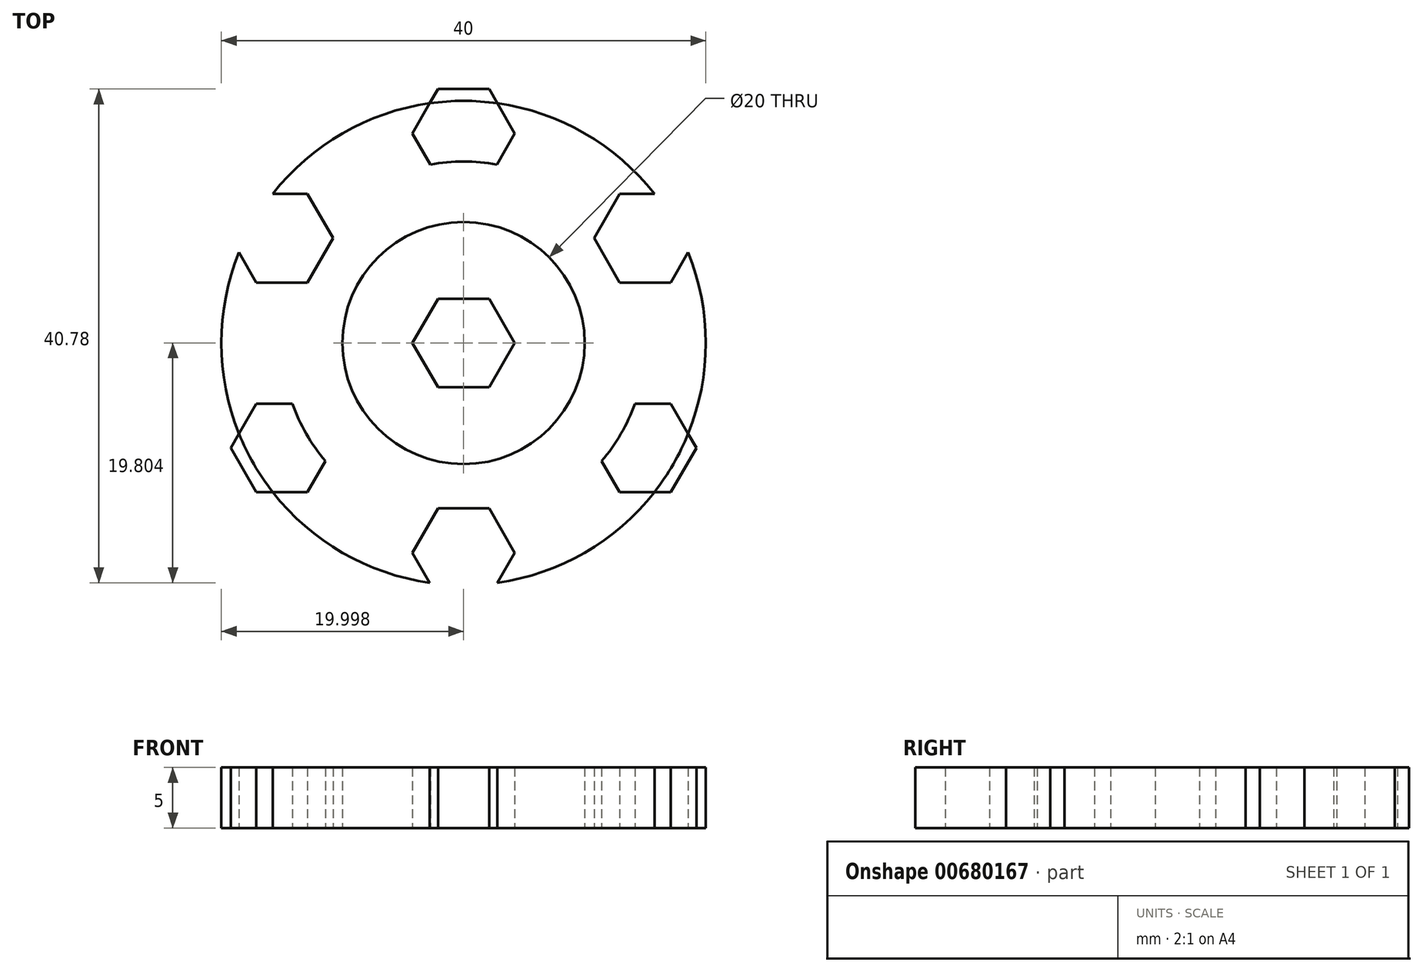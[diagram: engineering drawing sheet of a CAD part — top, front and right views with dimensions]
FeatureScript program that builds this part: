
annotation { "Feature Type Name" : "Feature", "Feature Type Description" : "" }
export const myFeature = defineFeature(function(context is Context, id is Id, definition is map)
    precondition{}
    {
        {
            var Q0;
            Q0=qCreatedBy(makeId("Top.planeOp"),FACE);
            var sketch = newSketch(context, id + "F0", { "sketchPlane" : qUnion([Q0])});
            skLineSegment(sketch, "E0.0", {"start": v(-11.35, 1.25) * mm, "end": v(-21.35, 1.25) * mm});
            skLineSegment(sketch, "E0.1", {"start": v(-21.35, 1.25) * mm, "end": v(-26.35, 9.91) * mm});
            skLineSegment(sketch, "E0.2", {"start": v(-26.35, 9.91) * mm, "end": v(-21.35, 18.57) * mm});
            skLineSegment(sketch, "E0.3", {"start": v(-21.35, 18.57) * mm, "end": v(-11.35, 18.57) * mm});
            skLineSegment(sketch, "E0.4", {"start": v(-11.35, 18.57) * mm, "end": v(-6.35, 9.91) * mm});
            skLineSegment(sketch, "E0.5", {"start": v(-6.35, 9.91) * mm, "end": v(-11.35, 1.25) * mm});
            skPoint(sketch, "E0.0.midPoint", {"position": v(-16.35, 1.25) * mm});
            skLineSegment(sketch, "E1", {"start": v(-21.35, 1.25) * mm, "end": v(-11.35, 1.25) * mm});
            skLineSegment(sketch, "E2", {"start": v(-11.35, 1.25) * mm, "end": v(-6.35, 9.91) * mm});
            skLineSegment(sketch, "E3", {"start": v(-6.35, 9.91) * mm, "end": v(-11.35, 18.57) * mm});
            skLineSegment(sketch, "E4", {"start": v(-11.35, 18.57) * mm, "end": v(-21.35, 18.57) * mm});
            skLineSegment(sketch, "E5", {"start": v(-21.35, 18.57) * mm, "end": v(-26.35, 9.91) * mm});
            skLineSegment(sketch, "E6", {"start": v(-26.35, 9.91) * mm, "end": v(-21.35, 1.25) * mm});
            skLineSegment(sketch, "E7.MirrorCS", {"start": v(-6.35, 27.23) * mm, "end": v(-11.35, 35.9) * mm});
            skLineSegment(sketch, "E8.MirrorCS", {"start": v(-21.35, 35.9) * mm, "end": v(-26.35, 27.23) * mm});
            skLineSegment(sketch, "E9.MirrorCS", {"start": v(-26.35, 27.23) * mm, "end": v(-21.35, 18.57) * mm});
            skLineSegment(sketch, "E10.MirrorCS", {"start": v(-11.35, 35.9) * mm, "end": v(-6.35, 27.23) * mm});
            skLineSegment(sketch, "E11.MirrorCS", {"start": v(-11.35, 35.9) * mm, "end": v(-21.35, 35.9) * mm});
            skLineSegment(sketch, "E12.MirrorCS", {"start": v(-11.35, 18.57) * mm, "end": v(-6.35, 27.23) * mm});
            skLineSegment(sketch, "E13.MirrorCS", {"start": v(-21.35, 35.9) * mm, "end": v(-11.35, 35.9) * mm});
            skLineSegment(sketch, "E14.MirrorCS", {"start": v(-6.35, 27.23) * mm, "end": v(-11.35, 18.57) * mm});
            skLineSegment(sketch, "E15.MirrorCS", {"start": v(-26.35, 27.23) * mm, "end": v(-21.35, 35.9) * mm});
            skLineSegment(sketch, "E16.MirrorCS", {"start": v(-21.35, 18.57) * mm, "end": v(-26.35, 27.23) * mm});
            skPoint(sketch, "E17.MirrorP", {"position": v(-16.35, 35.9) * mm});
            skLineSegment(sketch, "E18.MirrorCS", {"start": v(-6.35, 9.91) * mm, "end": v(3.65, 9.91) * mm});
            skLineSegment(sketch, "E19.MirrorCS", {"start": v(3.65, 9.91) * mm, "end": v(8.65, 18.57) * mm});
            skLineSegment(sketch, "E20.MirrorCS", {"start": v(8.65, 18.57) * mm, "end": v(3.65, 27.23) * mm});
            skLineSegment(sketch, "E21.MirrorCS", {"start": v(3.65, 27.23) * mm, "end": v(-6.35, 27.23) * mm});
            skLineSegment(sketch, "E22.MirrorCS", {"start": v(3.65, 9.91) * mm, "end": v(-6.35, 9.91) * mm});
            skPoint(sketch, "E23.MirrorP", {"position": v(6.15, 14.24) * mm});
            skLineSegment(sketch, "E24.MirrorCS", {"start": v(-6.35, 27.23) * mm, "end": v(3.65, 27.23) * mm});
            skLineSegment(sketch, "E25.MirrorCS", {"start": v(8.65, 18.57) * mm, "end": v(3.65, 9.91) * mm});
            skLineSegment(sketch, "E26.MirrorCS", {"start": v(3.65, 27.23) * mm, "end": v(8.65, 18.57) * mm});
            skLineSegment(sketch, "E27.MirrorCS", {"start": v(8.65, 1.25) * mm, "end": v(3.65, 9.91) * mm});
            skLineSegment(sketch, "E28.MirrorCS", {"start": v(3.65, -7.4) * mm, "end": v(8.65, 1.25) * mm});
            skLineSegment(sketch, "E29.MirrorCS", {"start": v(-6.35, -7.4) * mm, "end": v(3.65, -7.4) * mm});
            skLineSegment(sketch, "E30.MirrorCS", {"start": v(-11.35, 1.25) * mm, "end": v(-6.35, -7.4) * mm});
            skLineSegment(sketch, "E31.MirrorCS", {"start": v(3.65, 9.91) * mm, "end": v(8.65, 1.25) * mm});
            skPoint(sketch, "E32.MirrorP", {"position": v(-8.85, -3.08) * mm});
            skLineSegment(sketch, "E33.MirrorCS", {"start": v(3.65, -7.4) * mm, "end": v(-6.35, -7.4) * mm});
            skLineSegment(sketch, "E34.MirrorCS", {"start": v(-6.35, -7.4) * mm, "end": v(-11.35, 1.25) * mm});
            skLineSegment(sketch, "E35.MirrorCS", {"start": v(8.65, 1.25) * mm, "end": v(3.65, -7.4) * mm});
            skLineSegment(sketch, "E36.MirrorCS", {"start": v(-11.35, -16.07) * mm, "end": v(-6.35, -7.4) * mm});
            skLineSegment(sketch, "E37.MirrorCS", {"start": v(-6.35, -7.4) * mm, "end": v(-11.35, -16.07) * mm});
            skLineSegment(sketch, "E38.MirrorCS", {"start": v(-21.35, -16.07) * mm, "end": v(-11.35, -16.07) * mm});
            skLineSegment(sketch, "E39.MirrorCS", {"start": v(-21.35, 1.25) * mm, "end": v(-26.35, -7.4) * mm});
            skLineSegment(sketch, "E40.MirrorCS", {"start": v(-26.35, -7.4) * mm, "end": v(-21.35, -16.07) * mm});
            skLineSegment(sketch, "E41.MirrorCS", {"start": v(-11.35, -16.07) * mm, "end": v(-21.35, -16.07) * mm});
            skLineSegment(sketch, "E42.MirrorCS", {"start": v(-26.35, -7.4) * mm, "end": v(-21.35, 1.25) * mm});
            skLineSegment(sketch, "E43.MirrorCS", {"start": v(-21.35, -16.07) * mm, "end": v(-26.35, -7.4) * mm});
            skLineSegment(sketch, "E44.MirrorCS", {"start": v(-36.35, -7.4) * mm, "end": v(-26.35, -7.4) * mm});
            skLineSegment(sketch, "E45.MirrorCS", {"start": v(-41.35, 1.25) * mm, "end": v(-36.35, -7.4) * mm});
            skLineSegment(sketch, "E46.MirrorCS", {"start": v(-36.35, -7.4) * mm, "end": v(-41.35, 1.25) * mm});
            skLineSegment(sketch, "E47.MirrorCS", {"start": v(-26.35, -7.4) * mm, "end": v(-36.35, -7.4) * mm});
            skLineSegment(sketch, "E48.MirrorCS", {"start": v(-36.35, 9.91) * mm, "end": v(-41.35, 1.25) * mm});
            skLineSegment(sketch, "E49.MirrorCS", {"start": v(-41.35, 1.25) * mm, "end": v(-36.35, 9.91) * mm});
            skLineSegment(sketch, "E50.MirrorCS", {"start": v(-26.35, 9.91) * mm, "end": v(-36.35, 9.91) * mm});
            skLineSegment(sketch, "E51.MirrorCS", {"start": v(-36.35, 9.91) * mm, "end": v(-26.35, 9.91) * mm});
            skLineSegment(sketch, "E52.MirrorCS", {"start": v(-26.35, 27.23) * mm, "end": v(-36.35, 27.23) * mm});
            skLineSegment(sketch, "E53.MirrorCS", {"start": v(-36.35, 27.23) * mm, "end": v(-41.35, 18.57) * mm});
            skLineSegment(sketch, "E54.MirrorCS", {"start": v(-41.35, 18.57) * mm, "end": v(-36.35, 9.91) * mm});
            skLineSegment(sketch, "E55.MirrorCS", {"start": v(-41.35, 18.57) * mm, "end": v(-36.35, 27.23) * mm});
            skLineSegment(sketch, "E56.MirrorCS", {"start": v(-36.35, 27.23) * mm, "end": v(-26.35, 27.23) * mm});
            skPoint(sketch, "E57.MirrorP", {"position": v(-38.85, 14.24) * mm});
            skLineSegment(sketch, "E58.MirrorCS", {"start": v(-36.35, 9.91) * mm, "end": v(-41.35, 18.57) * mm});
            skLineSegment(sketch, "E59.MirrorCS", {"start": v(-26.35, 44.55) * mm, "end": v(-36.35, 44.55) * mm});
            skLineSegment(sketch, "E60.MirrorCS", {"start": v(-41.35, 35.9) * mm, "end": v(-36.35, 27.23) * mm});
            skLineSegment(sketch, "E61.MirrorCS", {"start": v(-36.35, 44.55) * mm, "end": v(-26.35, 44.55) * mm});
            skLineSegment(sketch, "E62.MirrorCS", {"start": v(-26.35, 44.55) * mm, "end": v(-21.35, 35.9) * mm});
            skLineSegment(sketch, "E63.MirrorCS", {"start": v(-36.35, 44.55) * mm, "end": v(-41.35, 35.9) * mm});
            skLineSegment(sketch, "E64.MirrorCS", {"start": v(-36.35, 27.23) * mm, "end": v(-41.35, 35.9) * mm});
            skLineSegment(sketch, "E65.MirrorCS", {"start": v(-21.35, 35.9) * mm, "end": v(-26.35, 44.55) * mm});
            skPoint(sketch, "E66.MirrorP", {"position": v(-38.85, 40.22) * mm});
            skLineSegment(sketch, "E67.MirrorCS", {"start": v(-41.35, 35.9) * mm, "end": v(-36.35, 44.55) * mm});
            skLineSegment(sketch, "E68.MirrorCS", {"start": v(-56.35, 9.91) * mm, "end": v(-51.35, 18.57) * mm});
            skLineSegment(sketch, "E69.MirrorCS", {"start": v(-41.35, 1.25) * mm, "end": v(-51.35, 1.25) * mm});
            skLineSegment(sketch, "E70.MirrorCS", {"start": v(-56.35, 9.91) * mm, "end": v(-51.35, 1.25) * mm});
            skLineSegment(sketch, "E71.MirrorCS", {"start": v(-51.35, 1.25) * mm, "end": v(-56.35, 9.91) * mm});
            skLineSegment(sketch, "E72.MirrorCS", {"start": v(-51.35, 18.57) * mm, "end": v(-56.35, 9.91) * mm});
            skLineSegment(sketch, "E73.MirrorCS", {"start": v(-51.35, 18.57) * mm, "end": v(-41.35, 18.57) * mm});
            skLineSegment(sketch, "E74.MirrorCS", {"start": v(-41.35, 18.57) * mm, "end": v(-51.35, 18.57) * mm});
            skLineSegment(sketch, "E75.MirrorCS", {"start": v(-51.35, 1.25) * mm, "end": v(-41.35, 1.25) * mm});
            skLineSegment(sketch, "E76.MirrorCS", {"start": v(-6.35, 44.55) * mm, "end": v(3.65, 44.55) * mm});
            skLineSegment(sketch, "E77.MirrorCS", {"start": v(3.65, 44.55) * mm, "end": v(-6.35, 44.55) * mm});
            skLineSegment(sketch, "E78.MirrorCS", {"start": v(8.65, 35.9) * mm, "end": v(3.65, 44.55) * mm});
            skLineSegment(sketch, "E79.MirrorCS", {"start": v(3.65, 44.55) * mm, "end": v(8.65, 35.9) * mm});
            skLineSegment(sketch, "E80.MirrorCS", {"start": v(8.65, 35.9) * mm, "end": v(3.65, 27.23) * mm});
            skLineSegment(sketch, "E81.MirrorCS", {"start": v(3.65, 27.23) * mm, "end": v(8.65, 35.9) * mm});
            skLineSegment(sketch, "E82.MirrorCS", {"start": v(-6.35, 44.55) * mm, "end": v(-11.35, 35.9) * mm});
            skLineSegment(sketch, "E83.MirrorCS", {"start": v(-11.35, 35.9) * mm, "end": v(-6.35, 44.55) * mm});
            skPoint(sketch, "E84.MirrorP", {"position": v(-8.85, 40.22) * mm});
            skLineSegment(sketch, "E85.MirrorCS", {"start": v(23.65, 9.91) * mm, "end": v(18.65, 18.57) * mm});
            skLineSegment(sketch, "E86.MirrorCS", {"start": v(18.65, 1.25) * mm, "end": v(23.65, 9.91) * mm});
            skLineSegment(sketch, "E87.MirrorCS", {"start": v(18.65, 18.57) * mm, "end": v(23.65, 9.91) * mm});
            skLineSegment(sketch, "E88.MirrorCS", {"start": v(23.65, 9.91) * mm, "end": v(18.65, 1.25) * mm});
            skLineSegment(sketch, "E89.MirrorCS", {"start": v(18.65, 1.25) * mm, "end": v(8.65, 1.25) * mm});
            skLineSegment(sketch, "E90.MirrorCS", {"start": v(18.65, 18.57) * mm, "end": v(8.65, 18.57) * mm});
            skLineSegment(sketch, "E91.MirrorCS", {"start": v(8.65, 1.25) * mm, "end": v(18.65, 1.25) * mm});
            skLineSegment(sketch, "E92.MirrorCS", {"start": v(8.65, 18.57) * mm, "end": v(18.65, 18.57) * mm});
            skLineSegment(sketch, "E93.MirrorCS", {"start": v(8.65, -16.07) * mm, "end": v(3.65, -24.73) * mm});
            skLineSegment(sketch, "E94.MirrorCS", {"start": v(3.65, -24.73) * mm, "end": v(8.65, -16.07) * mm});
            skLineSegment(sketch, "E95.MirrorCS", {"start": v(3.65, -24.73) * mm, "end": v(-6.35, -24.73) * mm});
            skLineSegment(sketch, "E96.MirrorCS", {"start": v(-6.35, -24.73) * mm, "end": v(3.65, -24.73) * mm});
            skLineSegment(sketch, "E97.MirrorCS", {"start": v(-6.35, -24.73) * mm, "end": v(-11.35, -16.07) * mm});
            skLineSegment(sketch, "E98.MirrorCS", {"start": v(-11.35, -16.07) * mm, "end": v(-6.35, -24.73) * mm});
            skPoint(sketch, "E99.MirrorP", {"position": v(-16.35, -16.07) * mm});
            skLineSegment(sketch, "E100.MirrorCS", {"start": v(8.65, -16.07) * mm, "end": v(3.65, -7.4) * mm});
            skPoint(sketch, "E101.MirrorP", {"position": v(-8.85, -11.74) * mm});
            skLineSegment(sketch, "E102.MirrorCS", {"start": v(3.65, -7.4) * mm, "end": v(8.65, -16.07) * mm});
            skLineSegment(sketch, "E103.MirrorCS", {"start": v(-26.35, -24.73) * mm, "end": v(-36.35, -24.73) * mm});
            skLineSegment(sketch, "E104.MirrorCS", {"start": v(-36.35, -24.73) * mm, "end": v(-26.35, -24.73) * mm});
            skLineSegment(sketch, "E105.MirrorCS", {"start": v(-36.35, -24.73) * mm, "end": v(-41.35, -16.07) * mm});
            skLineSegment(sketch, "E106.MirrorCS", {"start": v(-41.35, -16.07) * mm, "end": v(-36.35, -24.73) * mm});
            skLineSegment(sketch, "E107.MirrorCS", {"start": v(-41.35, -16.07) * mm, "end": v(-36.35, -7.4) * mm});
            skLineSegment(sketch, "E108.MirrorCS", {"start": v(-26.35, -24.73) * mm, "end": v(-21.35, -16.07) * mm});
            skPoint(sketch, "E109.MirrorP", {"position": v(-38.85, -11.74) * mm});
            skLineSegment(sketch, "E110.MirrorCS", {"start": v(-21.35, -16.07) * mm, "end": v(-26.35, -24.73) * mm});
            skPoint(sketch, "E111.MirrorP", {"position": v(-23.85, -20.4) * mm});
            skLineSegment(sketch, "E112.MirrorCS", {"start": v(-36.35, -7.4) * mm, "end": v(-41.35, -16.07) * mm});
            skPoint(sketch, "E113.MirrorP", {"position": v(-38.85, -20.4) * mm});
            skPoint(sketch, "E114.MirrorP", {"position": v(-31.35, -24.73) * mm});
            skLineSegment(sketch, "E115", {"start": v(-11.35, 18.57) * mm, "end": v(-21.35, 1.25) * mm});
            skLineSegment(sketch, "E116", {"start": v(-26.35, 9.91) * mm, "end": v(-6.35, 9.91) * mm});
            skLineSegment(sketch, "E117", {"start": v(-11.35, 1.25) * mm, "end": v(-21.35, 18.57) * mm});
            skPoint(sketch, "E118", {"position": v(-16.35, 9.91) * mm});
            skCircle(sketch, "E119", {"center": v(-16.35, 9.91) * mm, "radius": 15 * mm});
            skPoint(sketch, "E120", {"position": v(-31.35, 9.91) * mm});
            skPoint(sketch, "E121", {"position": v(-1.35, 9.91) * mm});
            skPoint(sketch, "E122", {"position": v(-23.85, -3.08) * mm});
            skPoint(sketch, "E123", {"position": v(-23.85, 22.9) * mm});
            skPoint(sketch, "E124", {"position": v(-8.85, 22.9) * mm});
            skLineSegment(sketch, "E125.0", {"start": v(-3.47, 39.55) * mm, "end": v(0.76, 39.55) * mm});
            skLineSegment(sketch, "E125.1", {"start": v(2.87, 35.9) * mm, "end": v(0.76, 32.23) * mm});
            skLineSegment(sketch, "E125.2", {"start": v(0.76, 32.23) * mm, "end": v(-3.47, 32.23) * mm});
            skLineSegment(sketch, "E125.3", {"start": v(0.76, 39.55) * mm, "end": v(2.87, 35.9) * mm});
            skLineSegment(sketch, "E125.4", {"start": v(-3.47, 32.23) * mm, "end": v(-5.58, 35.9) * mm});
            skLineSegment(sketch, "E125.5", {"start": v(-5.58, 35.9) * mm, "end": v(-3.47, 39.55) * mm});
            skLineSegment(sketch, "E126.0", {"start": v(0.76, 22.23) * mm, "end": v(-3.47, 22.23) * mm});
            skLineSegment(sketch, "E126.1", {"start": v(2.87, 18.57) * mm, "end": v(0.76, 14.91) * mm});
            skLineSegment(sketch, "E126.2", {"start": v(-3.47, 14.91) * mm, "end": v(0.76, 14.91) * mm});
            skLineSegment(sketch, "E126.3", {"start": v(0.76, 22.23) * mm, "end": v(2.87, 18.57) * mm});
            skLineSegment(sketch, "E126.4", {"start": v(-3.47, 14.91) * mm, "end": v(-5.58, 18.57) * mm});
            skLineSegment(sketch, "E126.5", {"start": v(-5.58, 18.57) * mm, "end": v(-3.47, 22.23) * mm});
            skLineSegment(sketch, "E127.0", {"start": v(-18.47, 30.9) * mm, "end": v(-20.58, 27.23) * mm});
            skLineSegment(sketch, "E127.1", {"start": v(-12.13, 27.23) * mm, "end": v(-14.24, 30.9) * mm});
            skLineSegment(sketch, "E127.2", {"start": v(-14.24, 23.57) * mm, "end": v(-12.13, 27.23) * mm});
            skLineSegment(sketch, "E127.3", {"start": v(-18.47, 30.9) * mm, "end": v(-14.24, 30.9) * mm});
            skLineSegment(sketch, "E127.4", {"start": v(-14.24, 23.57) * mm, "end": v(-18.47, 23.57) * mm});
            skLineSegment(sketch, "E127.5", {"start": v(-20.58, 27.23) * mm, "end": v(-18.47, 23.57) * mm});
            skLineSegment(sketch, "E128.0", {"start": v(-29.24, 39.55) * mm, "end": v(-27.13, 35.9) * mm});
            skLineSegment(sketch, "E128.1", {"start": v(-33.47, 32.23) * mm, "end": v(-29.24, 32.23) * mm});
            skLineSegment(sketch, "E128.2", {"start": v(-35.58, 35.9) * mm, "end": v(-33.47, 32.23) * mm});
            skLineSegment(sketch, "E128.3", {"start": v(-27.13, 35.9) * mm, "end": v(-29.24, 32.23) * mm});
            skLineSegment(sketch, "E128.4", {"start": v(-35.58, 35.9) * mm, "end": v(-33.47, 39.55) * mm});
            skLineSegment(sketch, "E128.5", {"start": v(-33.47, 39.55) * mm, "end": v(-29.24, 39.55) * mm});
            skLineSegment(sketch, "E129.0", {"start": v(17.87, 9.91) * mm, "end": v(15.76, 13.57) * mm});
            skLineSegment(sketch, "E129.1", {"start": v(11.53, 13.57) * mm, "end": v(9.42, 9.91) * mm});
            skLineSegment(sketch, "E129.2", {"start": v(9.42, 9.91) * mm, "end": v(11.53, 6.25) * mm});
            skLineSegment(sketch, "E129.3", {"start": v(15.76, 13.57) * mm, "end": v(11.53, 13.57) * mm});
            skLineSegment(sketch, "E129.4", {"start": v(11.53, 6.25) * mm, "end": v(15.76, 6.25) * mm});
            skLineSegment(sketch, "E129.5", {"start": v(15.76, 6.25) * mm, "end": v(17.87, 9.91) * mm});
            skCircle(sketch, "E130.0", {"center": v(-16.35, 9.91) * mm, "radius": 20 * mm});
            skCircle(sketch, "E131.0", {"center": v(-16.35, 9.91) * mm, "radius": 10 * mm});
            skLineSegment(sketch, "E132.0", {"start": v(-35.58, 18.57) * mm, "end": v(-33.47, 22.23) * mm});
            skLineSegment(sketch, "E132.1", {"start": v(-29.24, 22.23) * mm, "end": v(-27.13, 18.57) * mm});
            skLineSegment(sketch, "E132.2", {"start": v(-27.13, 18.57) * mm, "end": v(-29.24, 14.91) * mm});
            skLineSegment(sketch, "E132.3", {"start": v(-33.47, 22.23) * mm, "end": v(-29.24, 22.23) * mm});
            skLineSegment(sketch, "E132.4", {"start": v(-29.24, 14.91) * mm, "end": v(-33.47, 14.91) * mm});
            skLineSegment(sketch, "E132.5", {"start": v(-33.47, 14.91) * mm, "end": v(-35.58, 18.57) * mm});
            skLineSegment(sketch, "E133.0", {"start": v(-5.58, 1.25) * mm, "end": v(-3.47, 4.91) * mm});
            skLineSegment(sketch, "E133.1", {"start": v(0.76, 4.91) * mm, "end": v(2.87, 1.25) * mm});
            skLineSegment(sketch, "E133.2", {"start": v(2.87, 1.25) * mm, "end": v(0.76, -2.4) * mm});
            skLineSegment(sketch, "E133.3", {"start": v(-3.47, 4.91) * mm, "end": v(0.76, 4.91) * mm});
            skLineSegment(sketch, "E133.4", {"start": v(0.76, -2.4) * mm, "end": v(-3.47, -2.4) * mm});
            skLineSegment(sketch, "E133.5", {"start": v(-5.58, 1.25) * mm, "end": v(-3.47, -2.4) * mm});
            skLineSegment(sketch, "E134.0", {"start": v(-12.13, 9.91) * mm, "end": v(-14.24, 13.57) * mm});
            skLineSegment(sketch, "E134.1", {"start": v(-18.47, 13.57) * mm, "end": v(-20.58, 9.91) * mm});
            skLineSegment(sketch, "E134.2", {"start": v(-20.58, 9.91) * mm, "end": v(-18.47, 6.25) * mm});
            skLineSegment(sketch, "E134.3", {"start": v(-14.24, 13.57) * mm, "end": v(-18.47, 13.57) * mm});
            skLineSegment(sketch, "E134.4", {"start": v(-18.47, 6.25) * mm, "end": v(-14.24, 6.25) * mm});
            skLineSegment(sketch, "E134.5", {"start": v(-14.24, 6.25) * mm, "end": v(-12.13, 9.91) * mm});
            skLineSegment(sketch, "E135.0", {"start": v(-29.24, 4.91) * mm, "end": v(-27.13, 1.25) * mm});
            skLineSegment(sketch, "E135.1", {"start": v(-33.47, 4.91) * mm, "end": v(-35.58, 1.25) * mm});
            skLineSegment(sketch, "E135.2", {"start": v(-35.58, 1.25) * mm, "end": v(-33.47, -2.4) * mm});
            skLineSegment(sketch, "E135.3", {"start": v(-29.24, 4.91) * mm, "end": v(-33.47, 4.91) * mm});
            skLineSegment(sketch, "E135.4", {"start": v(-33.47, -2.4) * mm, "end": v(-29.24, -2.4) * mm});
            skLineSegment(sketch, "E135.5", {"start": v(-29.24, -2.4) * mm, "end": v(-27.13, 1.25) * mm});
            skLineSegment(sketch, "E136.0", {"start": v(-48.47, 13.57) * mm, "end": v(-50.58, 9.91) * mm});
            skLineSegment(sketch, "E136.1", {"start": v(-42.13, 9.91) * mm, "end": v(-44.24, 13.57) * mm});
            skLineSegment(sketch, "E136.2", {"start": v(-42.13, 9.91) * mm, "end": v(-44.24, 6.25) * mm});
            skLineSegment(sketch, "E136.3", {"start": v(-48.47, 13.57) * mm, "end": v(-44.24, 13.57) * mm});
            skLineSegment(sketch, "E136.4", {"start": v(-44.24, 6.25) * mm, "end": v(-48.47, 6.25) * mm});
            skLineSegment(sketch, "E136.5", {"start": v(-48.47, 6.25) * mm, "end": v(-50.58, 9.91) * mm});
            skLineSegment(sketch, "E137.0", {"start": v(-18.47, -11.07) * mm, "end": v(-20.58, -7.4) * mm});
            skLineSegment(sketch, "E137.1", {"start": v(-14.24, -11.07) * mm, "end": v(-12.13, -7.4) * mm});
            skLineSegment(sketch, "E137.2", {"start": v(-14.24, -3.75) * mm, "end": v(-12.13, -7.4) * mm});
            skLineSegment(sketch, "E137.3", {"start": v(-18.47, -11.07) * mm, "end": v(-14.24, -11.07) * mm});
            skLineSegment(sketch, "E137.4", {"start": v(-18.47, -3.75) * mm, "end": v(-14.24, -3.75) * mm});
            skLineSegment(sketch, "E137.5", {"start": v(-20.58, -7.4) * mm, "end": v(-18.47, -3.75) * mm});
            skLineSegment(sketch, "E138.0", {"start": v(-35.58, -16.07) * mm, "end": v(-33.47, -12.4) * mm});
            skLineSegment(sketch, "E138.1", {"start": v(-27.13, -16.07) * mm, "end": v(-29.24, -12.4) * mm});
            skLineSegment(sketch, "E138.2", {"start": v(-29.24, -19.73) * mm, "end": v(-27.13, -16.07) * mm});
            skLineSegment(sketch, "E138.3", {"start": v(-33.47, -12.4) * mm, "end": v(-29.24, -12.4) * mm});
            skLineSegment(sketch, "E138.4", {"start": v(-29.24, -19.73) * mm, "end": v(-33.47, -19.73) * mm});
            skLineSegment(sketch, "E138.5", {"start": v(-33.47, -19.73) * mm, "end": v(-35.58, -16.07) * mm});
            skLineSegment(sketch, "E139.0", {"start": v(2.87, -16.07) * mm, "end": v(0.76, -12.4) * mm});
            skLineSegment(sketch, "E139.1", {"start": v(-5.58, -16.07) * mm, "end": v(-3.47, -12.4) * mm});
            skLineSegment(sketch, "E139.2", {"start": v(-5.58, -16.07) * mm, "end": v(-3.47, -19.73) * mm});
            skLineSegment(sketch, "E139.3", {"start": v(0.76, -12.4) * mm, "end": v(-3.47, -12.4) * mm});
            skLineSegment(sketch, "E139.4", {"start": v(0.76, -19.73) * mm, "end": v(-3.47, -19.73) * mm});
            skLineSegment(sketch, "E139.5", {"start": v(2.87, -16.07) * mm, "end": v(0.76, -19.73) * mm});
            skSolve(sketch);
        }
        {
            var Q0;
            Q0=makeQuery(id+"F0.imprint","IMPRINT",FACE,{"disambiguationData":[TD([[makeQuery(id+"F0.imprint","IMPRINT",EDGE,{"derivedFrom":sQuery(id+"F0.wireOp",EDGE,"E38.MirrorCS")}),1.0]])]});
            var Q1;
            {var subQ0=sQuery(id+"F0.wireOp",EDGE,"E0.2");Q1=makeQuery(id+"F0.imprint","IMPRINT",FACE,{"disambiguationData":[TD([[makeQuery(id+"F0.imprint","IMPRINT",EDGE,{"derivedFrom":subQ0}),-1.0]])]});}
            var Q2;
            Q2=makeQuery(id+"F0.imprint","IMPRINT",FACE,{"disambiguationData":[TD([[makeQuery(id+"F0.imprint","IMPRINT",EDGE,{"derivedFrom":sQuery(id+"F0.wireOp",EDGE,"E55.MirrorCS")}),-1.0]])]});
            var Q3;
            Q3=makeQuery(id+"F0.imprint","IMPRINT",FACE,{"disambiguationData":[TD([[makeQuery(id+"F0.imprint","IMPRINT",EDGE,{"derivedFrom":sQuery(id+"F0.wireOp",EDGE,"E52.MirrorCS")}),-1.0]])]});
            var Q4;
            Q4=makeQuery(id+"F0.imprint","IMPRINT",FACE,{"disambiguationData":[TD([[makeQuery(id+"F0.imprint","IMPRINT",EDGE,{"derivedFrom":sQuery(id+"F0.wireOp",EDGE,"E49.MirrorCS")}),1.0]])]});
            var Q5;
            {var subQ13=sQuery(id+"F0.wireOp",EDGE,"E126.4");Q5=makeQuery(id+"F0.imprint","IMPRINT",FACE,{"disambiguationData":[TD([[makeQuery(id+"F0.imprint","IMPRINT",EDGE,{"derivedFrom":subQ13}),1.0]])]});}
            var Q6;
            Q6=makeQuery(id+"F0.imprint","IMPRINT",FACE,{"disambiguationData":[TD([[makeQuery(id+"F0.imprint","IMPRINT",EDGE,{"derivedFrom":sQuery(id+"F0.wireOp",EDGE,"E7.MirrorCS")}),-1.0]])]});
            var Q7;
            Q7=makeQuery(id+"F0.imprint","IMPRINT",FACE,{"disambiguationData":[TD([[makeQuery(id+"F0.imprint","IMPRINT",EDGE,{"derivedFrom":sQuery(id+"F0.wireOp",EDGE,"E19.MirrorCS")}),-1.0]])]});
            var Q8;
            {var subQ0=sQuery(id+"F0.wireOp",EDGE,"E0.4");Q8=makeQuery(id+"F0.imprint","IMPRINT",FACE,{"disambiguationData":[TD([[makeQuery(id+"F0.imprint","IMPRINT",EDGE,{"derivedFrom":subQ0}),-1.0]])]});}
            var Q9;
            Q9=makeQuery(id+"F0.imprint","IMPRINT",FACE,{"disambiguationData":[TD([[makeQuery(id+"F0.imprint","IMPRINT",EDGE,{"derivedFrom":sQuery(id+"F0.wireOp",EDGE,"E33.MirrorCS")}),1.0]])]});
            var Q10;
            {var subQ12=sQuery(id+"F0.wireOp",EDGE,"E132.2");Q10=makeQuery(id+"F0.imprint","IMPRINT",FACE,{"disambiguationData":[TD([[makeQuery(id+"F0.imprint","IMPRINT",EDGE,{"derivedFrom":subQ12}),1.0]])]});}
            var Q11;
            Q11=makeQuery(id+"F0.imprint","IMPRINT",FACE,{"disambiguationData":[TD([[makeQuery(id+"F0.imprint","IMPRINT",EDGE,{"derivedFrom":sQuery(id+"F0.wireOp",EDGE,"E104.MirrorCS")}),1.0]])]});
            var Q12;
            Q12=makeQuery(id+"F0.imprint","IMPRINT",FACE,{"disambiguationData":[TD([[makeQuery(id+"F0.imprint","IMPRINT",EDGE,{"derivedFrom":sQuery(id+"F0.wireOp",EDGE,"E45.MirrorCS")}),1.0]])]});
            var Q13;
            Q13=makeQuery(id+"F0.imprint","IMPRINT",FACE,{"disambiguationData":[TD([[makeQuery(id+"F0.imprint","IMPRINT",EDGE,{"derivedFrom":sQuery(id+"F0.wireOp",EDGE,"E26.MirrorCS")}),-1.0]])]});
            var Q14;
            Q14=makeQuery(id+"F0.imprint","IMPRINT",FACE,{"disambiguationData":[TD([[makeQuery(id+"F0.imprint","IMPRINT",EDGE,{"derivedFrom":sQuery(id+"F0.wireOp",EDGE,"E13.MirrorCS")}),-1.0]])]});
            var Q15;
            Q15=makeQuery(id+"F0.imprint","IMPRINT",FACE,{"disambiguationData":[TD([[makeQuery(id+"F0.imprint","IMPRINT",EDGE,{"derivedFrom":sQuery(id+"F0.wireOp",EDGE,"E35.MirrorCS")}),-1.0]])]});
            var Q16;
            {var subQ1=sQuery(id+"F0.wireOp",EDGE,"E16.MirrorCS");var subQ7=sQuery(id+"F0.wireOp",EDGE,"E119");var subQ9=makeQuery(id+"F0.imprint","INTERSECT",VERTEX,{"derivedFrom":[subQ1,subQ7]});Q16=makeQuery(id+"F0.imprint","IMPRINT",FACE,{"disambiguationData":[TD([[makeQuery(id+"F0.imprint","IMPRINT",EDGE,{"disambiguationData":[TD([[subQ9,-1.0]])],"derivedFrom":subQ7}),-1.0]])]});}
            var Q17;
            {var subQ3=sQuery(id+"F0.wireOp",EDGE,"E119");var subQ5=sQuery(id+"F0.wireOp",EDGE,"E51.MirrorCS");var subQ6=makeQuery(id+"F0.imprint","INTERSECT",VERTEX,{"derivedFrom":[subQ5,subQ3]});Q17=makeQuery(id+"F0.imprint","IMPRINT",FACE,{"disambiguationData":[TD([[makeQuery(id+"F0.imprint","IMPRINT",EDGE,{"disambiguationData":[TD([[subQ6,1.0]])],"derivedFrom":subQ3}),-1.0]])]});}
            var Q18;
            {var subQ5=sQuery(id+"F0.wireOp",EDGE,"E133.0");Q18=makeQuery(id+"F0.imprint","IMPRINT",FACE,{"disambiguationData":[TD([[makeQuery(id+"F0.imprint","IMPRINT",EDGE,{"derivedFrom":subQ5}),1.0]])]});}
            var Q19;
            {var subQ5=sQuery(id+"F0.wireOp",EDGE,"E51.MirrorCS");var subQ7=sQuery(id+"F0.wireOp",EDGE,"E119");var subQ8=makeQuery(id+"F0.imprint","INTERSECT",VERTEX,{"derivedFrom":[subQ5,subQ7]});Q19=makeQuery(id+"F0.imprint","IMPRINT",FACE,{"disambiguationData":[TD([[makeQuery(id+"F0.imprint","IMPRINT",EDGE,{"disambiguationData":[TD([[subQ8,-1.0]])],"derivedFrom":subQ7}),-1.0]])]});}
            var Q20;
            {var subQ13=sQuery(id+"F0.wireOp",EDGE,"E137.4");Q20=makeQuery(id+"F0.imprint","IMPRINT",FACE,{"disambiguationData":[TD([[makeQuery(id+"F0.imprint","IMPRINT",EDGE,{"derivedFrom":subQ13}),1.0]])]});}
            var Q21;
            {var subQ5=sQuery(id+"F0.wireOp",EDGE,"E12.MirrorCS");var subQ7=sQuery(id+"F0.wireOp",EDGE,"E119");var subQ8=makeQuery(id+"F0.imprint","INTERSECT",VERTEX,{"derivedFrom":[subQ5,subQ7]});Q21=makeQuery(id+"F0.imprint","IMPRINT",FACE,{"disambiguationData":[TD([[makeQuery(id+"F0.imprint","IMPRINT",EDGE,{"disambiguationData":[TD([[subQ8,1.0]])],"derivedFrom":subQ7}),-1.0]])]});}
            var Q22;
            {var subQ11=sQuery(id+"F0.wireOp",EDGE,"E135.0");Q22=makeQuery(id+"F0.imprint","IMPRINT",FACE,{"disambiguationData":[TD([[makeQuery(id+"F0.imprint","IMPRINT",EDGE,{"derivedFrom":subQ11}),1.0]])]});}
            var Q23;
            {var subQ5=sQuery(id+"F0.wireOp",EDGE,"E127.4");Q23=makeQuery(id+"F0.imprint","IMPRINT",FACE,{"disambiguationData":[TD([[makeQuery(id+"F0.imprint","IMPRINT",EDGE,{"derivedFrom":subQ5}),1.0]])]});}
            var Q24;
            {var subQ5=sQuery(id+"F0.wireOp",EDGE,"E119");var subQ6=sQuery(id+"F0.wireOp",EDGE,"E22.MirrorCS");var subQ7=makeQuery(id+"F0.imprint","INTERSECT",VERTEX,{"derivedFrom":[subQ6,subQ5]});Q24=makeQuery(id+"F0.imprint","IMPRINT",FACE,{"disambiguationData":[TD([[makeQuery(id+"F0.imprint","IMPRINT",EDGE,{"disambiguationData":[TD([[subQ7,-1.0]])],"derivedFrom":subQ5}),-1.0]])]});}
            var Q25;
            {var subQ1=sQuery(id+"F0.wireOp",EDGE,"E42.MirrorCS");var subQ5=sQuery(id+"F0.wireOp",EDGE,"E119");var subQ6=makeQuery(id+"F0.imprint","INTERSECT",VERTEX,{"derivedFrom":[subQ1,subQ5]});Q25=makeQuery(id+"F0.imprint","IMPRINT",FACE,{"disambiguationData":[TD([[makeQuery(id+"F0.imprint","IMPRINT",EDGE,{"disambiguationData":[TD([[subQ6,1.0]])],"derivedFrom":subQ5}),-1.0]])]});}
            var Q26;
            {var subQ5=sQuery(id+"F0.wireOp",EDGE,"E30.MirrorCS");var subQ7=sQuery(id+"F0.wireOp",EDGE,"E119");var subQ8=makeQuery(id+"F0.imprint","INTERSECT",VERTEX,{"derivedFrom":[subQ5,subQ7]});Q26=makeQuery(id+"F0.imprint","IMPRINT",FACE,{"disambiguationData":[TD([[makeQuery(id+"F0.imprint","IMPRINT",EDGE,{"disambiguationData":[TD([[subQ8,-1.0]])],"derivedFrom":subQ7}),-1.0]])]});}
            var Q27;
            {var subQ5=sQuery(id+"F0.wireOp",EDGE,"E22.MirrorCS");var subQ7=sQuery(id+"F0.wireOp",EDGE,"E119");var subQ9=makeQuery(id+"F0.imprint","INTERSECT",VERTEX,{"derivedFrom":[subQ5,subQ7]});Q27=makeQuery(id+"F0.imprint","IMPRINT",FACE,{"disambiguationData":[TD([[makeQuery(id+"F0.imprint","IMPRINT",EDGE,{"disambiguationData":[TD([[subQ9,1.0]])],"derivedFrom":subQ7}),-1.0]])]});}
            var Q28;
            {var subQ0=sQuery(id+"F0.wireOp",EDGE,"E119");var subQ1=sQuery(id+"F0.wireOp",EDGE,"E42.MirrorCS");var subQ2=makeQuery(id+"F0.imprint","INTERSECT",VERTEX,{"derivedFrom":[subQ1,subQ0]});Q28=makeQuery(id+"F0.imprint","IMPRINT",FACE,{"disambiguationData":[TD([[makeQuery(id+"F0.imprint","IMPRINT",EDGE,{"disambiguationData":[TD([[subQ2,-1.0]])],"derivedFrom":subQ0}),-1.0]])]});}
            var Q29;
            {var subQ3=sQuery(id+"F0.wireOp",EDGE,"E119");var subQ7=sQuery(id+"F0.wireOp",EDGE,"E12.MirrorCS");var subQ8=makeQuery(id+"F0.imprint","INTERSECT",VERTEX,{"derivedFrom":[subQ7,subQ3]});Q29=makeQuery(id+"F0.imprint","IMPRINT",FACE,{"disambiguationData":[TD([[makeQuery(id+"F0.imprint","IMPRINT",EDGE,{"disambiguationData":[TD([[subQ8,-1.0]])],"derivedFrom":subQ3}),-1.0]])]});}
            var Q30;
            {var subQ3=sQuery(id+"F0.wireOp",EDGE,"E119");var subQ7=sQuery(id+"F0.wireOp",EDGE,"E16.MirrorCS");var subQ8=makeQuery(id+"F0.imprint","INTERSECT",VERTEX,{"derivedFrom":[subQ7,subQ3]});Q30=makeQuery(id+"F0.imprint","IMPRINT",FACE,{"disambiguationData":[TD([[makeQuery(id+"F0.imprint","IMPRINT",EDGE,{"disambiguationData":[TD([[subQ8,1.0]])],"derivedFrom":subQ3}),-1.0]])]});}
            var Q31;
            {var subQ0=sQuery(id+"F0.wireOp",EDGE,"E0.0");Q31=makeQuery(id+"F0.imprint","IMPRINT",FACE,{"disambiguationData":[TD([[makeQuery(id+"F0.imprint","IMPRINT",EDGE,{"derivedFrom":subQ0}),-1.0]])]});}
            var Q32;
            {var subQ5=sQuery(id+"F0.wireOp",EDGE,"E30.MirrorCS");var subQ7=sQuery(id+"F0.wireOp",EDGE,"E119");var subQ8=makeQuery(id+"F0.imprint","INTERSECT",VERTEX,{"derivedFrom":[subQ5,subQ7]});Q32=makeQuery(id+"F0.imprint","IMPRINT",FACE,{"disambiguationData":[TD([[makeQuery(id+"F0.imprint","IMPRINT",EDGE,{"disambiguationData":[TD([[subQ8,1.0]])],"derivedFrom":subQ7}),-1.0]])]});}
            var Q33;
            {var subQ0=sQuery(id+"F0.wireOp",EDGE,"E134.0");Q33=makeQuery(id+"F0.imprint","IMPRINT",FACE,{"disambiguationData":[TD([[makeQuery(id+"F0.imprint","IMPRINT",EDGE,{"derivedFrom":subQ0}),1.0]])]});}
            var Q34;
            {var subQ0=sQuery(id+"F0.wireOp",EDGE,"E134.3");Q34=makeQuery(id+"F0.imprint","IMPRINT",FACE,{"disambiguationData":[TD([[makeQuery(id+"F0.imprint","IMPRINT",EDGE,{"derivedFrom":subQ0}),1.0]])]});}
            var Q35;
            {var subQ0=sQuery(id+"F0.wireOp",EDGE,"E134.1");Q35=makeQuery(id+"F0.imprint","IMPRINT",FACE,{"disambiguationData":[TD([[makeQuery(id+"F0.imprint","IMPRINT",EDGE,{"derivedFrom":subQ0}),1.0]])]});}
            var Q36;
            {var subQ0=sQuery(id+"F0.wireOp",EDGE,"E134.5");Q36=makeQuery(id+"F0.imprint","IMPRINT",FACE,{"disambiguationData":[TD([[makeQuery(id+"F0.imprint","IMPRINT",EDGE,{"derivedFrom":subQ0}),1.0]])]});}
            var Q37;
            {var subQ0=sQuery(id+"F0.wireOp",EDGE,"E134.2");Q37=makeQuery(id+"F0.imprint","IMPRINT",FACE,{"disambiguationData":[TD([[makeQuery(id+"F0.imprint","IMPRINT",EDGE,{"derivedFrom":subQ0}),1.0]])]});}
            var Q38;
            {var subQ0=sQuery(id+"F0.wireOp",EDGE,"E134.4");Q38=makeQuery(id+"F0.imprint","IMPRINT",FACE,{"disambiguationData":[TD([[makeQuery(id+"F0.imprint","IMPRINT",EDGE,{"derivedFrom":subQ0}),1.0]])]});}
            var Q39;
            {var subQ0=sQuery(id+"F0.wireOp",EDGE,"E0.2");Q39=makeQuery(id+"F0.imprint","IMPRINT",FACE,{"disambiguationData":[TD([[makeQuery(id+"F0.imprint","IMPRINT",EDGE,{"derivedFrom":subQ0}),1.0]])]});}
            var Q40;
            {var subQ0=sQuery(id+"F0.wireOp",EDGE,"E0.0");Q40=makeQuery(id+"F0.imprint","IMPRINT",FACE,{"disambiguationData":[TD([[makeQuery(id+"F0.imprint","IMPRINT",EDGE,{"derivedFrom":subQ0}),1.0]])]});}
            var Q41;
            {var subQ0=sQuery(id+"F0.wireOp",EDGE,"E0.4");Q41=makeQuery(id+"F0.imprint","IMPRINT",FACE,{"disambiguationData":[TD([[makeQuery(id+"F0.imprint","IMPRINT",EDGE,{"derivedFrom":subQ0}),1.0]])]});}
            var Q42;
            {var subQ5=sQuery(id+"F0.wireOp",EDGE,"E133.0");Q42=makeQuery(id+"F0.imprint","IMPRINT",FACE,{"disambiguationData":[TD([[makeQuery(id+"F0.imprint","IMPRINT",EDGE,{"derivedFrom":subQ5}),-1.0]])]});}
            var Q43;
            {var subQ5=sQuery(id+"F0.wireOp",EDGE,"E133.2");Q43=makeQuery(id+"F0.imprint","IMPRINT",FACE,{"disambiguationData":[TD([[makeQuery(id+"F0.imprint","IMPRINT",EDGE,{"derivedFrom":subQ5}),-1.0]])]});}
            var Q44;
            {var subQ0=sQuery(id+"F0.wireOp",EDGE,"E127.3");Q44=makeQuery(id+"F0.imprint","IMPRINT",FACE,{"disambiguationData":[TD([[makeQuery(id+"F0.imprint","IMPRINT",EDGE,{"derivedFrom":subQ0}),-1.0]])]});}
            var Q45;
            {var subQ5=sQuery(id+"F0.wireOp",EDGE,"E127.4");Q45=makeQuery(id+"F0.imprint","IMPRINT",FACE,{"disambiguationData":[TD([[makeQuery(id+"F0.imprint","IMPRINT",EDGE,{"derivedFrom":subQ5}),-1.0]])]});}
            var Q46;
            {var subQ5=sQuery(id+"F0.wireOp",EDGE,"E135.2");Q46=makeQuery(id+"F0.imprint","IMPRINT",FACE,{"disambiguationData":[TD([[makeQuery(id+"F0.imprint","IMPRINT",EDGE,{"derivedFrom":subQ5}),1.0]])]});}
            var Q47;
            {var subQ5=sQuery(id+"F0.wireOp",EDGE,"E135.0");Q47=makeQuery(id+"F0.imprint","IMPRINT",FACE,{"disambiguationData":[TD([[makeQuery(id+"F0.imprint","IMPRINT",EDGE,{"derivedFrom":subQ5}),-1.0]])]});}
            extrude(context, id + "F1", {"entities" : qUnion([Q0, Q1, Q2, Q3, Q4, Q5, Q6, Q7, Q8, Q9, Q10, Q11, Q12, Q13, Q14, Q15, Q16, Q17, Q18, Q19, Q20, Q21, Q22, Q23, Q24, Q25, Q26, Q27, Q28, Q29, Q30, Q31, Q32, Q33, Q34, Q35, Q36, Q37, Q38, Q39, Q40, Q41, Q42, Q43, Q44, Q45, Q46, Q47]), "depth" : 5 * mm, "offsetDistance" : 25 * mm});
        }
    });
